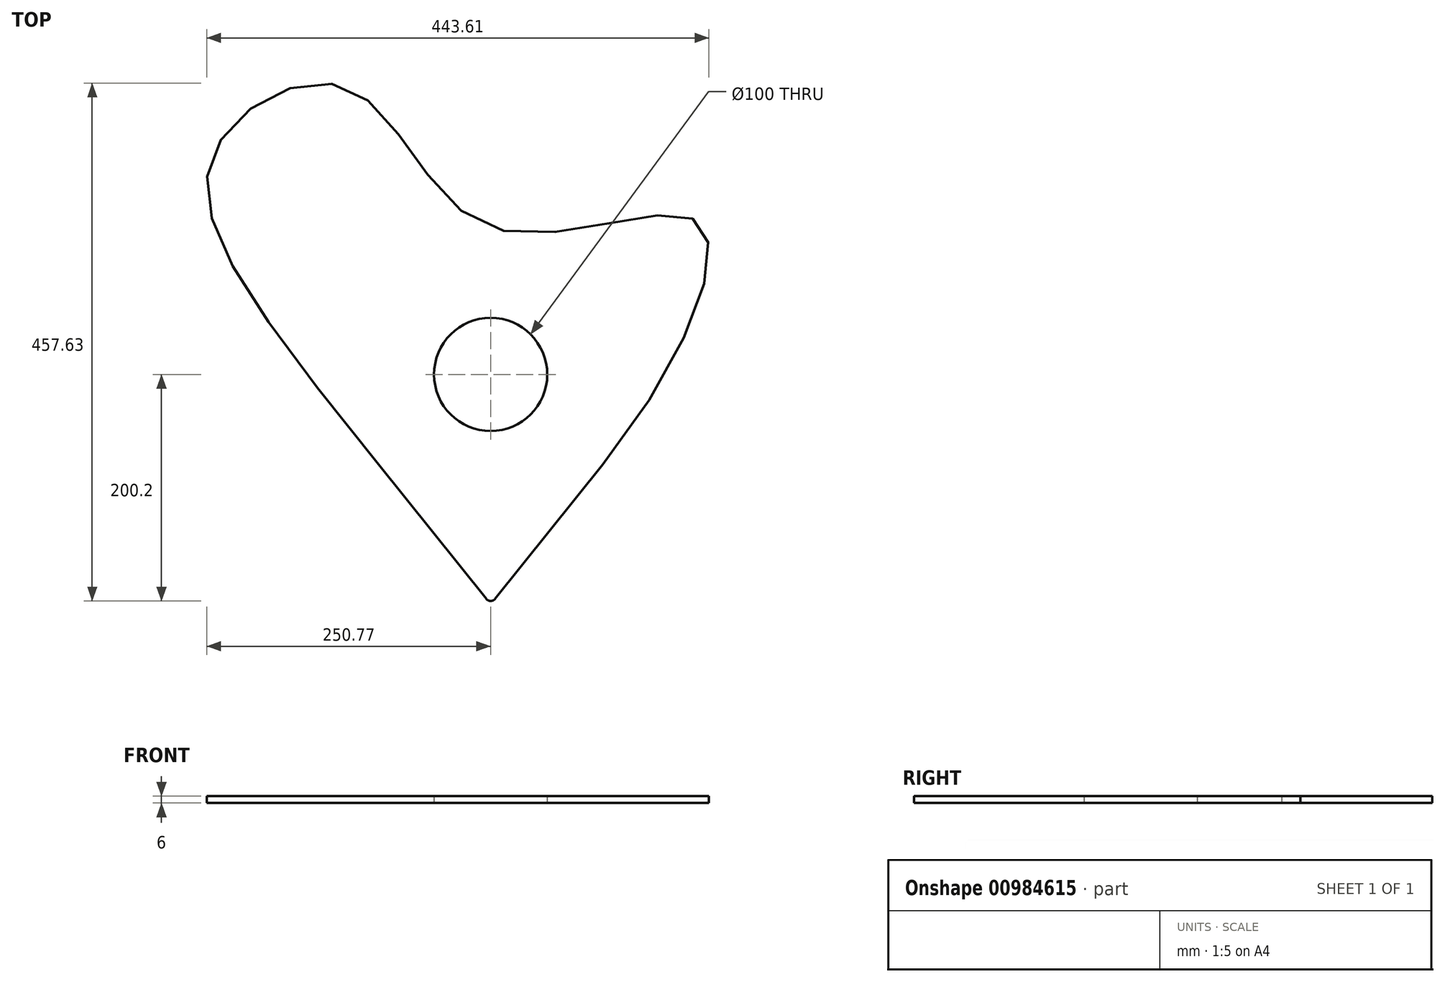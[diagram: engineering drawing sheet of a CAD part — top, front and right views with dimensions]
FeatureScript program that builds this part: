
annotation { "Feature Type Name" : "Feature", "Feature Type Description" : "" }
export const myFeature = defineFeature(function(context is Context, id is Id, definition is map)
    precondition{}
    {
        {
            var Q0;
            Q0=qCreatedBy(makeId("Top.planeOp"),FACE);
            var sketch = newSketch(context, id + "F0", { "sketchPlane" : qUnion([Q0])});
            skLineSegment(sketch, "E0", {"start": v(0, 0) * mm, "end": v(0, 254) * mm, "construction": true});
            skArc(sketch, "E1", {"start": v(0, 254) * mm, "mid": v(-114.48, 182) * mm, "end": v(-99.14, 47.62) * mm});
            skLineSegment(sketch, "E2", {"start": v(0, 0) * mm, "end": v(0, -76.2) * mm, "construction": true});
            skLineSegment(sketch, "E3", {"start": v(-99.14, 47.62) * mm, "end": v(-3.9, -71.32) * mm});
            skArc(sketch, "E4.MirrorCS", {"start": v(0, 254) * mm, "mid": v(114.48, 182) * mm, "end": v(99.14, 47.62) * mm});
            skLineSegment(sketch, "E5.MirrorCS", {"start": v(99.14, 47.62) * mm, "end": v(3.9, -71.33) * mm});
            skPoint(sketch, "E6.visualSharp", {"position": v(0, -76.2) * mm});
            skArc(sketch, "E6.filletArc", {"start": v(-3.9, -71.33) * mm, "mid": v(0, -73.2) * mm, "end": v(3.9, -71.33) * mm});
            skSolve(sketch);
        }
        {
            var Q0;
            Q0=makeQuery(id+"F0.imprint","IMPRINT",FACE,{"disambiguationData":[TD([[makeQuery(id+"F0.imprint","IMPRINT",EDGE,{"derivedFrom":sQuery(id+"F0.wireOp",EDGE,"E1")}),1.0]])]});
            extrude(context, id + "F1", {"entities" : qUnion([Q0]), "depth" : 6 * mm, "offsetDistance" : 25.4 * mm});
        }
        {
            var Q0;
            Q0=qCreatedBy(makeId("Top.planeOp"),FACE);
            var sketch = newSketch(context, id + "F2", { "sketchPlane" : qUnion([Q0])});
            skLineSegment(sketch, "E7", {"start": v(0, 0) * mm, "end": v(0, 254) * mm, "construction": true});
            skCircle(sketch, "E8", {"center": v(0, 127) * mm, "radius": 50 * mm});
            skSolve(sketch);
        }
        {
            var Q0;
            Q0=qCreatedBy(makeId("Top.planeOp"),FACE);
            var sketch = newSketch(context, id + "F3", { "sketchPlane" : qUnion([Q0])});
            skFitSpline(sketch, "E9", {"points": [v(-98.96, 47.4) * mm, v(-243.15, 326.23) * mm, v(-126.2, 380.05) * mm, v(0, 256.93) * mm, v(180.22, 263.62) * mm, v(99.14, 47.62) * mm], "startDerivative": vector(-1344.75, 1679.58) * mm, "endDerivative": vector(-1037.8, -1296.22) * mm});
            skLineSegment(sketch, "E10", {"start": v(-98.96, 47.4) * mm, "end": v(99.14, 47.62) * mm});
            skSolve(sketch);
        }
        {
            var Q0;
            Q0 = qSketchRegion(id + "F3", true);
            extrude(context, id + "F4", {"entities" : qUnion([Q0]), "operationType" : NewBodyOperationType.ADD, "depth" : 6 * mm, "offsetDistance" : 25 * mm});
        }
        {
            var Q0;
            Q0=makeQuery(id+"F2.imprint","IMPRINT",FACE,{"disambiguationData":[TD([[makeQuery(id+"F2.imprint","IMPRINT",EDGE,{"derivedFrom":sQuery(id+"F2.wireOp",EDGE,"E8")}),1.0]])]});
            extrude(context, id + "F5", {"entities" : qUnion([Q0]), "operationType" : NewBodyOperationType.REMOVE, "depth" : 25 * mm, "offsetDistance" : 25 * mm});
        }
    });
